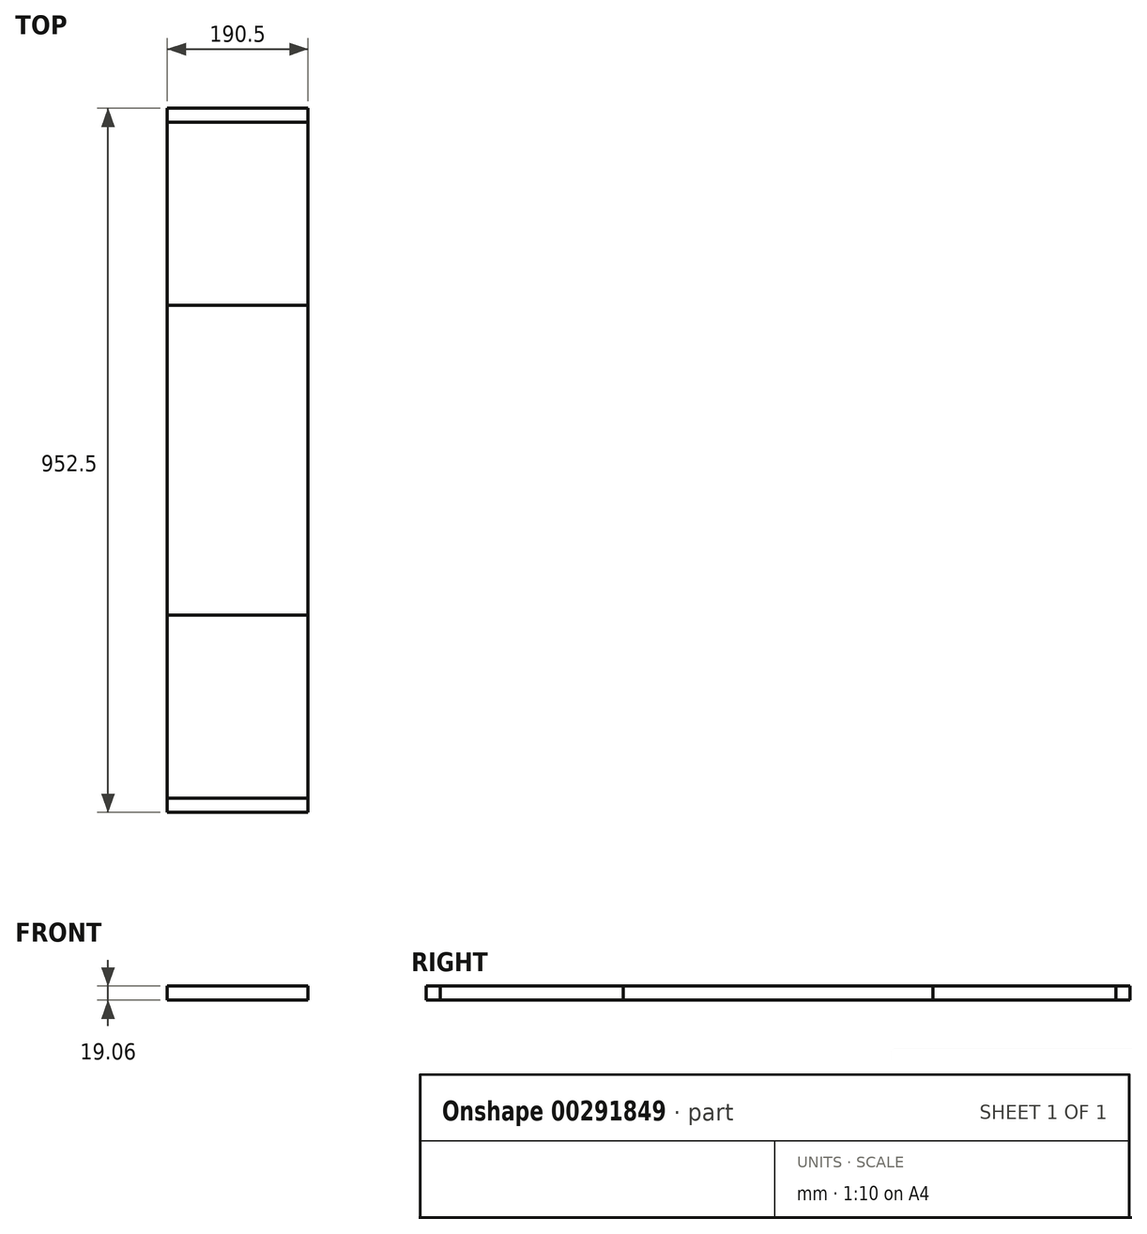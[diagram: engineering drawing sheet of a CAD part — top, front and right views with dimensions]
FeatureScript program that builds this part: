
annotation { "Feature Type Name" : "Feature", "Feature Type Description" : "" }
export const myFeature = defineFeature(function(context is Context, id is Id, definition is map)
    precondition{}
    {
        {
            var Q0;
            Q0=qCreatedBy(makeId("Front.planeOp"),FACE);
            var sketch = newSketch(context, id + "F0", { "sketchPlane" : qUnion([Q0])});
            skLineSegment(sketch, "E0.bottom", {"start": v(95.25, -9.53) * mm, "end": v(-95.25, -9.53) * mm});
            skLineSegment(sketch, "E0.top", {"start": v(95.25, 9.53) * mm, "end": v(-95.25, 9.53) * mm});
            skLineSegment(sketch, "E0.left", {"start": v(95.25, -9.53) * mm, "end": v(95.25, 9.53) * mm});
            skLineSegment(sketch, "E0.right", {"start": v(-95.25, -9.53) * mm, "end": v(-95.25, 9.52) * mm});
            skPoint(sketch, "E0.middle", {"position": v(0, 0) * mm});
            skSolve(sketch);
        }
        {
            var Q0;
            Q0 = qSketchRegion(id + "F0", true);
            extrude(context, id + "F1", {"entities" : qUnion([Q0]), "endBound" : BoundingType.SYMMETRIC, "depth" : 419.1 * mm});
        }
        {
            var Q0;
            Q0 = qSketchRegion(id + "F0", true);
            extrude(context, id + "F2", {"entities" : qUnion([Q0]), "endBound" : BoundingType.SYMMETRIC, "depth" : 914.4 * mm});
        }
        {
            var Q0;
            Q0 = qSketchRegion(id + "F0", true);
            extrude(context, id + "F3", {"entities" : qUnion([Q0]), "endBound" : BoundingType.SYMMETRIC, "depth" : 952.5 * mm});
        }
    });
